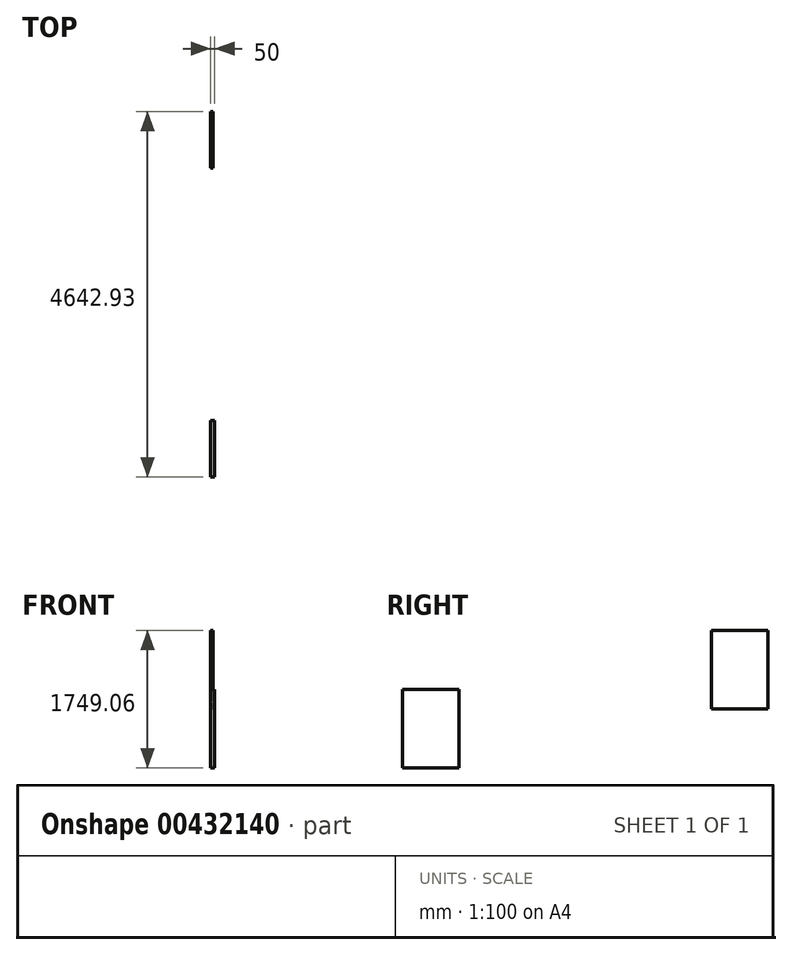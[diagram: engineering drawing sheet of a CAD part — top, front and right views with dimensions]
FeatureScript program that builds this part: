
annotation { "Feature Type Name" : "Feature", "Feature Type Description" : "" }
export const myFeature = defineFeature(function(context is Context, id is Id, definition is map)
    precondition{}
    {
        {
            var Q0;
            Q0=qCreatedBy(makeId("Right.planeOp"),FACE);
            var sketch = newSketch(context, id + "F0", { "sketchPlane" : qUnion([Q0])});
            skLineSegment(sketch, "E0.bottom", {"start": v(457.07, 506.39) * mm, "end": v(-262.93, 506.39) * mm});
            skLineSegment(sketch, "E0.top", {"start": v(457.07, -493.61) * mm, "end": v(-262.93, -493.61) * mm});
            skLineSegment(sketch, "E0.left", {"start": v(457.07, 506.39) * mm, "end": v(457.07, -493.61) * mm});
            skLineSegment(sketch, "E0.right", {"start": v(-262.93, 506.39) * mm, "end": v(-262.93, -493.61) * mm});
            skSolve(sketch);
        }
        {
            var Q0;
            Q0 = qSketchRegion(id + "F0", true);
            extrude(context, id + "F1", {"entities" : qUnion([Q0]), "depth" : 50 * mm});
        }
        {
            var Q0;
            Q0=makeQuery(id+"F0.imprint","IMPRINT",FACE,{"disambiguationData":[TD([[makeQuery(id+"F0.imprint","IMPRINT",EDGE,{"derivedFrom":sQuery(id+"F0.wireOp",EDGE,"E0.bottom")}),1.0]])]});
            var sketch = newSketch(context, id + "F2", { "sketchPlane" : qUnion([Q0])});
            skLineSegment(sketch, "E1.bottom", {"start": v(4380, 1255.45) * mm, "end": v(3660, 1255.45) * mm});
            skLineSegment(sketch, "E1.top", {"start": v(4380, 255.45) * mm, "end": v(3660, 255.45) * mm});
            skLineSegment(sketch, "E1.left", {"start": v(4380, 1255.45) * mm, "end": v(4380, 255.45) * mm});
            skLineSegment(sketch, "E1.right", {"start": v(3660, 1255.45) * mm, "end": v(3660, 255.45) * mm});
            skSolve(sketch);
        }
        {
            var Q0;
            Q0 = qSketchRegion(id + "F2", true);
            extrude(context, id + "F3", {"entities" : qUnion([Q0]), "depth" : 30 * mm});
        }
    });
